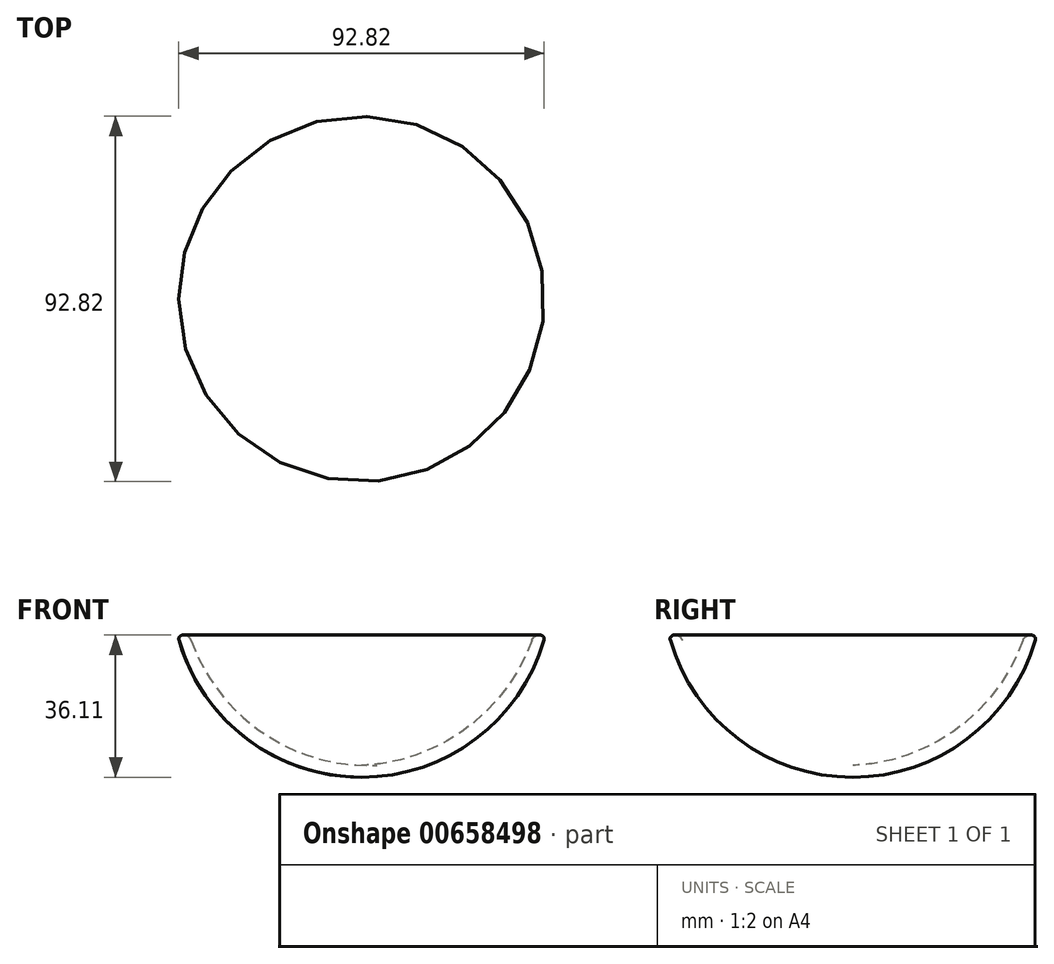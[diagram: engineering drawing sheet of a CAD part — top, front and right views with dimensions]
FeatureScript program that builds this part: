
annotation { "Feature Type Name" : "Feature", "Feature Type Description" : "" }
export const myFeature = defineFeature(function(context is Context, id is Id, definition is map)
    precondition{}
    {
        {
            var Q0;
            Q0=qCreatedBy(makeId("Front.planeOp"),FACE);
            var sketch = newSketch(context, id + "F0", { "sketchPlane" : qUnion([Q0])});
            skArc(sketch, "E0", {"start": v(0, 0) * mm, "mid": v(29.53, 10.08) * mm, "end": v(46.73, 36.11) * mm});
            skLineSegment(sketch, "E1", {"start": v(46.73, 36.11) * mm, "end": v(43.73, 36.11) * mm});
            skArc(sketch, "E2", {"start": v(0, 3) * mm, "mid": v(27.05, 12.7) * mm, "end": v(43.73, 36.11) * mm});
            skLineSegment(sketch, "E3", {"start": v(0, 3) * mm, "end": v(0, 0) * mm});
            skSolve(sketch);
        }
        {
            var Q0;
            Q0 = qSketchRegion(id + "F0", true);
            var Q1;
            Q1=sQuery(id+"F0.wireOp",EDGE,"E3");
            revolve(context, id + "F1", {"entities" : qUnion([Q0]), "axis" : qUnion([Q1]), "revolveType" : RevolveType.FULL});
        }
        {
            var Q0;
            Q0=makeQuery(id+"F1.opRevolve","SWEPT_EDGE",EDGE,{"disambiguationData":[OSD([sQuery(id+"F0.wireOp",EDGE,"E0"),sQuery(id+"F0.wireOp",EDGE,"E1")])]});
            fillet(context, id + "F2", {"entities" : qUnion([Q0]), "radius" : 1 * mm, "tangentPropagation" : true, "allowEdgeOverflow" : false});
        }
        {
            var Q0;
            Q0=makeQuery(id+"F1.opRevolve","SWEPT_EDGE",EDGE,{"disambiguationData":[OSD([sQuery(id+"F0.wireOp",EDGE,"E1"),sQuery(id+"F0.wireOp",EDGE,"E2")])]});
            fillet(context, id + "F3", {"entities" : qUnion([Q0]), "radius" : 2 * mm, "tangentPropagation" : true, "allowEdgeOverflow" : false});
        }
    });
